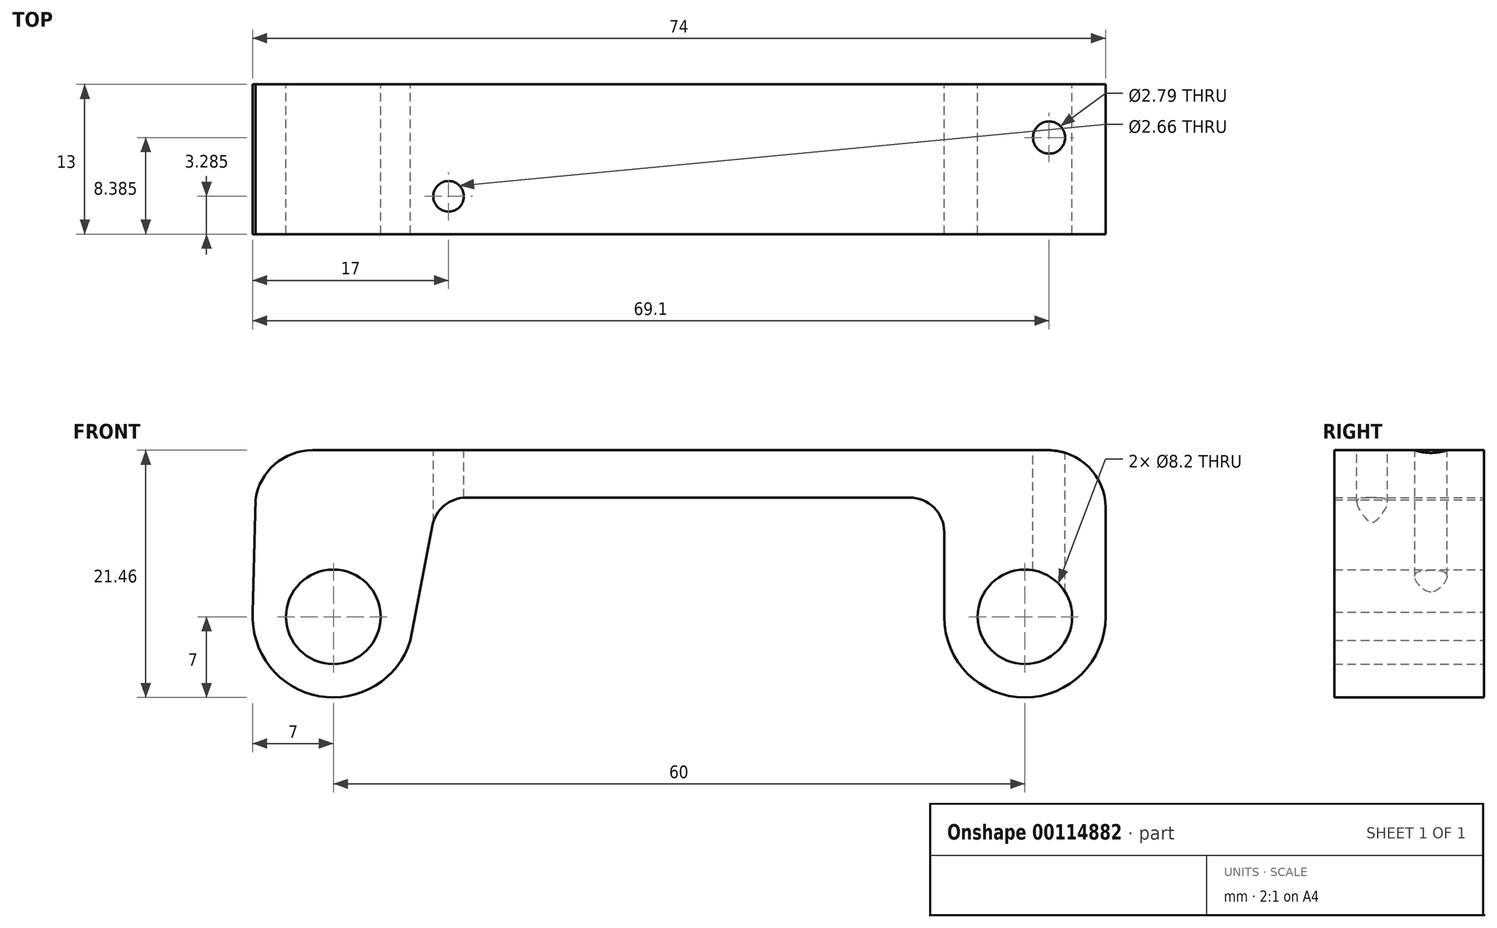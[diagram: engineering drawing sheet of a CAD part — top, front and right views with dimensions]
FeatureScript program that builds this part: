
annotation { "Feature Type Name" : "Feature", "Feature Type Description" : "" }
export const myFeature = defineFeature(function(context is Context, id is Id, definition is map)
    precondition{}
    {
        {
            var Q0;
            Q0=qCreatedBy(makeId("Front.planeOp"),FACE);
            var sketch = newSketch(context, id + "F0", { "sketchPlane" : qUnion([Q0])});
            skCircle(sketch, "E0", {"center": v(-30, 0) * mm, "radius": 4.1 * mm});
            skArc(sketch, "E1", {"start": v(-36.99, 0.4) * mm, "mid": v(-31.23, -6.9) * mm, "end": v(-23.3, -2.04) * mm});
            skArc(sketch, "E2.MirrorC", {"start": v(37, 0) * mm, "mid": v(30, -7) * mm, "end": v(23, 0) * mm});
            skCircle(sketch, "E3.MirrorC", {"center": v(30, 0) * mm, "radius": 4.1 * mm});
            skLineSegment(sketch, "E4.bottom", {"start": v(-31.8, 14.46) * mm, "end": v(1.21, 14.46) * mm});
            skLineSegment(sketch, "E5.MirrorCS", {"start": v(32, 14.46) * mm, "end": v(-1.21, 14.46) * mm});
            skLineSegment(sketch, "E6", {"start": v(37, 9.46) * mm, "end": v(37, 0) * mm});
            skLineSegment(sketch, "E7", {"start": v(-23.3, -2.04) * mm, "end": v(-21.4, 7.9) * mm});
            skLineSegment(sketch, "E8", {"start": v(23, 0) * mm, "end": v(23, 7.35) * mm});
            skLineSegment(sketch, "E9.trimOffspring", {"start": v(-18.45, 10.35) * mm, "end": v(-9.23, 10.35) * mm});
            skLineSegment(sketch, "E10.trimOffspring", {"start": v(20, 10.35) * mm, "end": v(10, 10.35) * mm});
            skArc(sketch, "E11.filletArc", {"start": v(-31.8, 14.46) * mm, "mid": v(-35.09, 13.23) * mm, "end": v(-36.76, 10.15) * mm});
            skArc(sketch, "E12.filletArc", {"start": v(37, 9.46) * mm, "mid": v(35.54, 13) * mm, "end": v(32, 14.46) * mm});
            skPoint(sketch, "E13.visualSharp", {"position": v(23, 10.35) * mm});
            skArc(sketch, "E13.filletArc", {"start": v(23, 7.35) * mm, "mid": v(22.12, 9.47) * mm, "end": v(20, 10.35) * mm});
            skPoint(sketch, "E14.visualSharp", {"position": v(-20.93, 10.35) * mm});
            skArc(sketch, "E14.filletArc", {"start": v(-18.45, 10.35) * mm, "mid": v(-20.37, 9.66) * mm, "end": v(-21.4, 7.9) * mm});
            skPoint(sketch, "E15.end.orphan", {"position": v(-36.26, 0) * mm});
            skLineSegment(sketch, "E16", {"start": v(-36.76, 10.15) * mm, "end": v(-36.99, 0.4) * mm});
            skLineSegment(sketch, "E17", {"start": v(-9.23, 10.35) * mm, "end": v(0, 10.35) * mm});
            skLineSegment(sketch, "E18", {"start": v(10, 10.35) * mm, "end": v(0, 10.35) * mm});
            skSolve(sketch);
        }
        {
            var Q0;
            Q0 = qSketchRegion(id + "F0", true);
            extrude(context, id + "F1", {"entities" : qUnion([Q0]), "depth" : 13 * mm});
        }
        {
            var Q0;
            Q0=makeQuery(id+"F1.opExtrude","SWEPT_FACE",FACE,{"disambiguationData":[OSD([sQuery(id+"F0.wireOp",EDGE,"E4.bottom"),sQuery(id+"F0.wireOp",EDGE,"E5.MirrorCS")])]});
            var sketch = newSketch(context, id + "F2", { "sketchPlane" : qUnion([Q0])});
            skCircle(sketch, "E19", {"center": v(-20, -9.72) * mm, "radius": 1.33 * mm});
            skCircle(sketch, "E20", {"center": v(32.1, -4.62) * mm, "radius": 1.4 * mm});
            skSolve(sketch);
        }
        {
            var Q0;
            Q0 = qSketchRegion(id + "F2", true);
            extrude(context, id + "F3", {"entities" : qUnion([Q0]), "operationType" : NewBodyOperationType.REMOVE, "oppositeDirection" : true, "depth" : 15 * mm});
        }
    });
